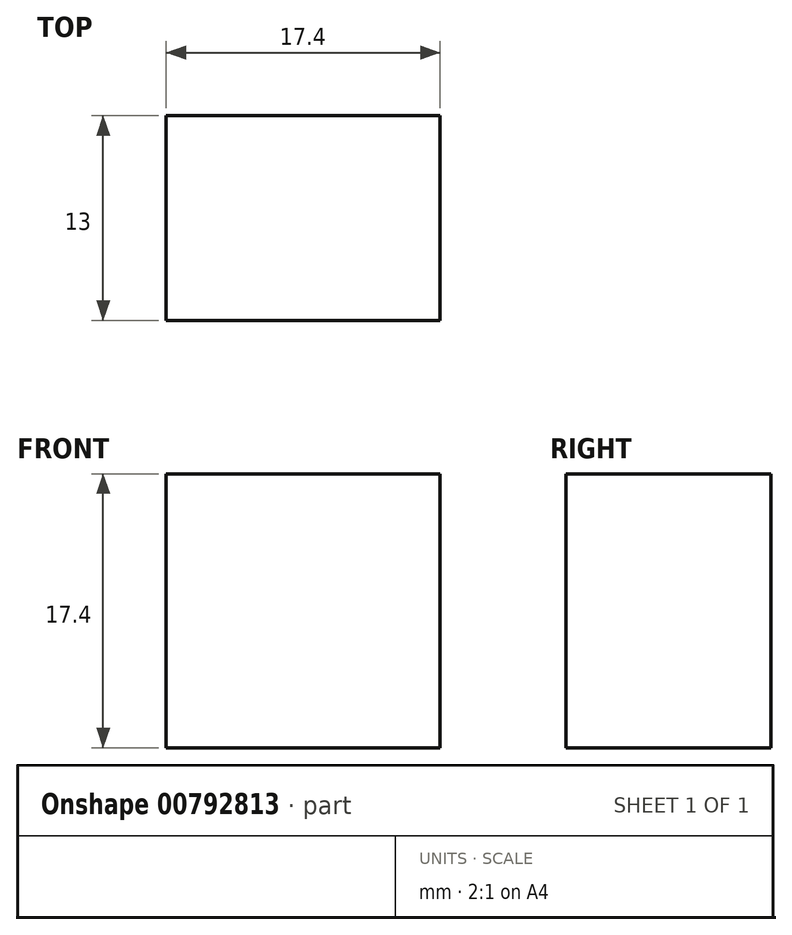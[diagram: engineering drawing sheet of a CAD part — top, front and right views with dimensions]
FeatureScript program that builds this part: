
annotation { "Feature Type Name" : "Feature", "Feature Type Description" : "" }
export const myFeature = defineFeature(function(context is Context, id is Id, definition is map)
    precondition{}
    {
        {
            var Q0;
            Q0=qCreatedBy(makeId("Top.planeOp"),FACE);
            var sketch = newSketch(context, id + "F0", { "sketchPlane" : qUnion([Q0])});
            skLineSegment(sketch, "E0.bottom", {"start": v(8.7, 6.5) * mm, "end": v(-8.7, 6.5) * mm});
            skLineSegment(sketch, "E0.top", {"start": v(8.7, -6.5) * mm, "end": v(-8.7, -6.5) * mm});
            skLineSegment(sketch, "E0.left", {"start": v(8.7, 6.5) * mm, "end": v(8.7, -6.5) * mm});
            skLineSegment(sketch, "E0.right", {"start": v(-8.7, 6.5) * mm, "end": v(-8.7, -6.5) * mm});
            skPoint(sketch, "E0.middle", {"position": v(0, 0) * mm});
            skSolve(sketch);
        }
        {
            var Q0;
            Q0 = qSketchRegion(id + "F0", true);
            extrude(context, id + "F1", {"entities" : qUnion([Q0]), "depth" : 17.4 * mm, "offsetDistance" : 25 * mm});
        }
    });
